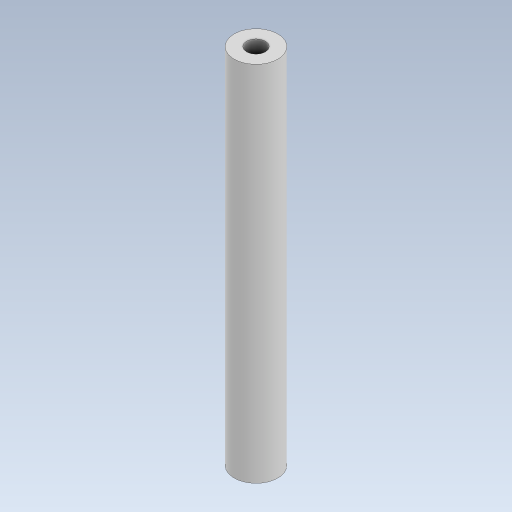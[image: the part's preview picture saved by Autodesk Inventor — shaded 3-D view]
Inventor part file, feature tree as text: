
AUTODESK INVENTOR PART (.ipt)
format: ipt  version: 2023.5 (Build 275446000, 446)  size: 80,896 bytes
history: native  units: mm
features: extrude x1, sketch x1
ambient origin geometry x8: Origin, YZ Plane, XZ Plane, XY Plane, X Axis, Y Axis, Z Axis, Center Point
bodies: Solid1 (feature_tree)
feature tree (2):
  extrude  "Extrusion1"  Depth=58.0mm
  sketch  "Sketch1"  dims[d0=7.0mm d1=3.0mm d2=58.0mm d3=0.0mm]
